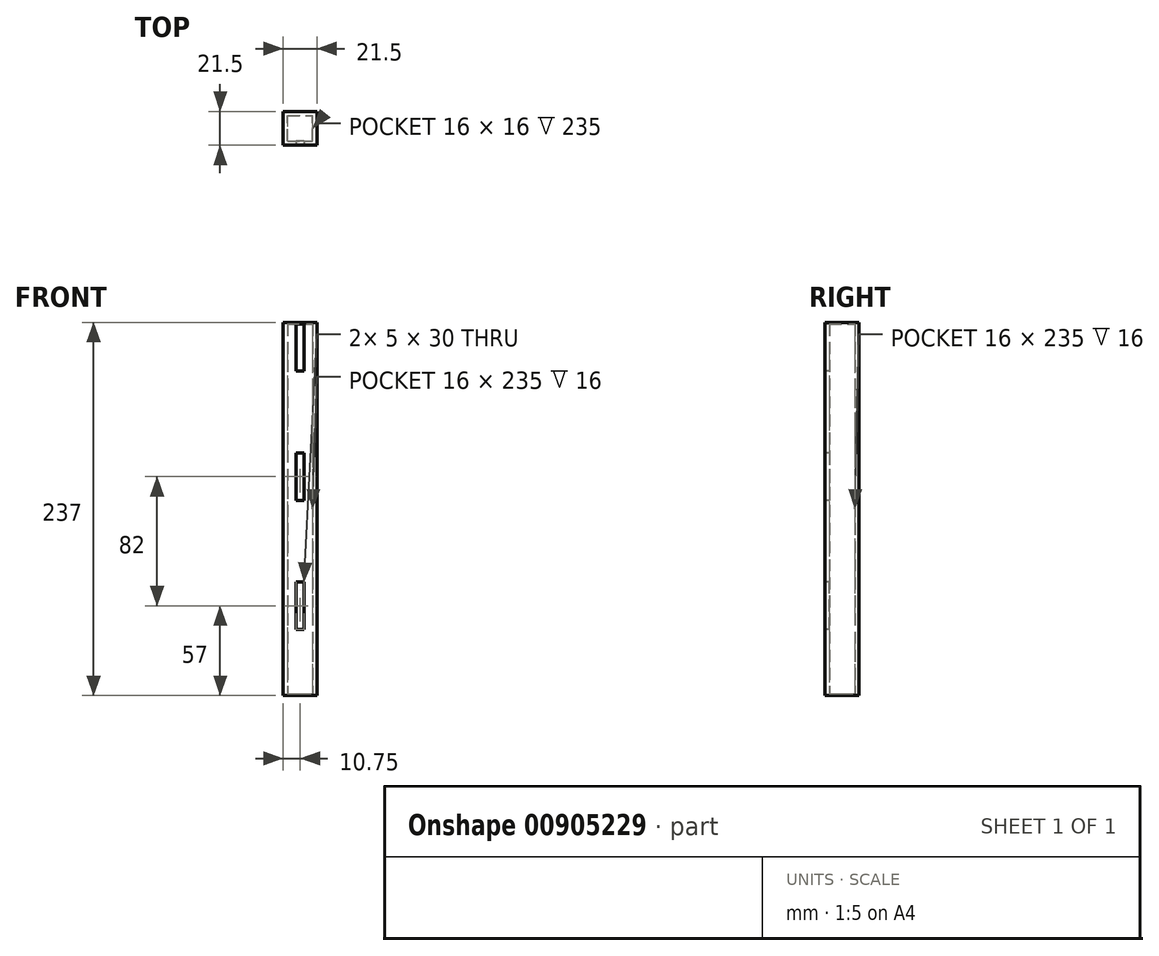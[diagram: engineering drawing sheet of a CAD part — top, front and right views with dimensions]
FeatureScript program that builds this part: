
annotation { "Feature Type Name" : "Feature", "Feature Type Description" : "" }
export const myFeature = defineFeature(function(context is Context, id is Id, definition is map)
    precondition{}
    {
        {
            var Q0;
            Q0=qCreatedBy(makeId("Top.planeOp"),FACE);
            var sketch = newSketch(context, id + "F0", { "sketchPlane" : qUnion([Q0])});
            skLineSegment(sketch, "E0.bottom", {"start": v(-21.5, 21.5) * mm, "end": v(0, 21.5) * mm});
            skLineSegment(sketch, "E0.top", {"start": v(-21.5, 0) * mm, "end": v(0, 0) * mm});
            skLineSegment(sketch, "E0.left", {"start": v(-21.5, 21.5) * mm, "end": v(-21.5, 0) * mm});
            skLineSegment(sketch, "E0.right", {"start": v(0, 21.5) * mm, "end": v(0, 0) * mm});
            skLineSegment(sketch, "E1.bottom", {"start": v(-18.75, 18.75) * mm, "end": v(-2.75, 18.75) * mm});
            skLineSegment(sketch, "E1.top", {"start": v(-18.75, 2.75) * mm, "end": v(-2.75, 2.75) * mm});
            skLineSegment(sketch, "E1.left", {"start": v(-18.75, 18.75) * mm, "end": v(-18.75, 2.75) * mm});
            skLineSegment(sketch, "E1.right", {"start": v(-2.75, 18.75) * mm, "end": v(-2.75, 2.75) * mm});
            skSolve(sketch);
        }
        {
            var Q0;
            Q0=makeQuery(id+"F0.imprint","IMPRINT",FACE,{"disambiguationData":[TD([[makeQuery(id+"F0.imprint","IMPRINT",EDGE,{"derivedFrom":sQuery(id+"F0.wireOp",EDGE,"E0.bottom")}),-1.0]])]});
            var Q1;
            Q1=makeQuery(id+"F0.imprint","IMPRINT",FACE,{"disambiguationData":[TD([[makeQuery(id+"F0.imprint","IMPRINT",EDGE,{"derivedFrom":sQuery(id+"F0.wireOp",EDGE,"E1.bottom")}),-1.0]])]});
            extrude(context, id + "F1", {"entities" : qUnion([Q0, Q1]), "depth" : 237 * mm, "offsetDistance" : 25 * mm});
        }
        {
            var Q0;
            Q0=makeQuery(id+"F1.opExtrude","SWEPT_FACE",FACE,{"disambiguationData":[OSD([sQuery(id+"F0.wireOp",EDGE,"E0.top")])]});
            var sketch = newSketch(context, id + "F2", { "sketchPlane" : qUnion([Q0])});
            skLineSegment(sketch, "E2.bottom", {"start": v(-7.25, 237) * mm, "end": v(-14.25, 237) * mm});
            skLineSegment(sketch, "E2.top", {"start": v(-7.25, 205) * mm, "end": v(-14.25, 205) * mm});
            skLineSegment(sketch, "E2.left", {"start": v(-7.25, 237) * mm, "end": v(-7.25, 205) * mm});
            skLineSegment(sketch, "E2.right", {"start": v(-14.25, 237) * mm, "end": v(-14.25, 205) * mm});
            skLineSegment(sketch, "E3.bottom", {"start": v(-8.25, 236) * mm, "end": v(-13.25, 236) * mm});
            skLineSegment(sketch, "E3.top", {"start": v(-8.25, 206) * mm, "end": v(-13.25, 206) * mm});
            skLineSegment(sketch, "E3.left", {"start": v(-8.25, 236) * mm, "end": v(-8.25, 206) * mm});
            skLineSegment(sketch, "E3.right", {"start": v(-13.25, 236) * mm, "end": v(-13.25, 206) * mm});
            skLineSegment(sketch, "E4", {"start": v(-62.73, 139) * mm, "end": v(121.74, 139) * mm});
            skLineSegment(sketch, "E5.bottom", {"start": v(-14.25, 155) * mm, "end": v(-7.25, 155) * mm});
            skLineSegment(sketch, "E5.top", {"start": v(-14.25, 139) * mm, "end": v(-7.25, 139) * mm});
            skLineSegment(sketch, "E5.left", {"start": v(-14.25, 155) * mm, "end": v(-14.25, 139) * mm});
            skLineSegment(sketch, "E5.right", {"start": v(-7.25, 155) * mm, "end": v(-7.25, 139) * mm});
            skLineSegment(sketch, "E6.bottom", {"start": v(-13.25, 154) * mm, "end": v(-8.25, 154) * mm});
            skLineSegment(sketch, "E6.top", {"start": v(-13.25, 139) * mm, "end": v(-8.25, 139) * mm});
            skLineSegment(sketch, "E6.left", {"start": v(-13.25, 154) * mm, "end": v(-13.25, 139) * mm});
            skLineSegment(sketch, "E6.right", {"start": v(-8.25, 154) * mm, "end": v(-8.25, 139) * mm});
            skLineSegment(sketch, "E7.MirrorCS", {"start": v(-7.25, 41) * mm, "end": v(-7.25, 73) * mm});
            skLineSegment(sketch, "E8.MirrorCS", {"start": v(-7.25, 73) * mm, "end": v(-14.25, 73) * mm});
            skLineSegment(sketch, "E9.MirrorCS", {"start": v(-7.25, 41) * mm, "end": v(-14.25, 41) * mm});
            skLineSegment(sketch, "E10.MirrorCS", {"start": v(-14.25, 41) * mm, "end": v(-14.25, 73) * mm});
            skLineSegment(sketch, "E11.MirrorCS", {"start": v(-8.25, 72) * mm, "end": v(-13.25, 72) * mm});
            skLineSegment(sketch, "E12.MirrorCS", {"start": v(-13.25, 42) * mm, "end": v(-13.25, 72) * mm});
            skLineSegment(sketch, "E13.MirrorCS", {"start": v(-8.25, 42) * mm, "end": v(-8.25, 72) * mm});
            skLineSegment(sketch, "E14.MirrorCS", {"start": v(-8.25, 42) * mm, "end": v(-13.25, 42) * mm});
            skLineSegment(sketch, "E15.MirrorCS", {"start": v(-8.25, 124) * mm, "end": v(-8.25, 139) * mm});
            skLineSegment(sketch, "E16.MirrorCS", {"start": v(-13.25, 124) * mm, "end": v(-8.25, 124) * mm});
            skLineSegment(sketch, "E17.MirrorCS", {"start": v(-14.25, 123) * mm, "end": v(-14.25, 139) * mm});
            skLineSegment(sketch, "E18.MirrorCS", {"start": v(-14.25, 123) * mm, "end": v(-7.25, 123) * mm});
            skLineSegment(sketch, "E19.MirrorCS", {"start": v(-7.25, 123) * mm, "end": v(-7.25, 139) * mm});
            skLineSegment(sketch, "E20.MirrorCS", {"start": v(-13.25, 124) * mm, "end": v(-13.25, 139) * mm});
            skSolve(sketch);
        }
        {
            var Q0;
            Q0=makeQuery(id+"F2.imprint","IMPRINT",FACE,{"disambiguationData":[TD([[makeQuery(id+"F2.imprint","IMPRINT",EDGE,{"derivedFrom":sQuery(id+"F2.wireOp",EDGE,"E3.bottom")}),1.0]])]});
            var Q1;
            Q1=makeQuery(id+"F2.imprint","IMPRINT",FACE,{"disambiguationData":[TD([[makeQuery(id+"F2.imprint","IMPRINT",EDGE,{"derivedFrom":sQuery(id+"F2.wireOp",EDGE,"E6.bottom")}),-1.0]])]});
            var Q2;
            Q2=makeQuery(id+"F2.imprint","IMPRINT",FACE,{"disambiguationData":[TD([[makeQuery(id+"F2.imprint","IMPRINT",EDGE,{"derivedFrom":sQuery(id+"F2.wireOp",EDGE,"E15.MirrorCS")}),1.0]])]});
            var Q3;
            Q3=makeQuery(id+"F2.imprint","IMPRINT",FACE,{"disambiguationData":[TD([[makeQuery(id+"F2.imprint","IMPRINT",EDGE,{"derivedFrom":sQuery(id+"F2.wireOp",EDGE,"E11.MirrorCS")}),1.0]])]});
            extrude(context, id + "F3", {"entities" : qUnion([Q0, Q1, Q2, Q3]), "operationType" : NewBodyOperationType.REMOVE, "oppositeDirection" : true, "depth" : 2.75 * mm, "offsetDistance" : 25 * mm});
        }
        {
            var Q0;
            Q0=makeQuery(id+"F1.opExtrude","CAP_FACE",FACE,{"disambiguationData":[OSD([sQuery(id+"F0.wireOp",EDGE,"E0.bottom"),sQuery(id+"F0.wireOp",EDGE,"E0.top"),sQuery(id+"F0.wireOp",EDGE,"E0.left"),sQuery(id+"F0.wireOp",EDGE,"E0.right")])],"isStart":true});
            var sketch = newSketch(context, id + "F4", { "sketchPlane" : qUnion([Q0])});
            skLineSegment(sketch, "E21.bottom", {"start": v(-18.75, -2.75) * mm, "end": v(-2.75, -2.75) * mm});
            skLineSegment(sketch, "E21.top", {"start": v(-18.75, -18.75) * mm, "end": v(-2.75, -18.75) * mm});
            skLineSegment(sketch, "E21.left", {"start": v(-18.75, -2.75) * mm, "end": v(-18.75, -18.75) * mm});
            skLineSegment(sketch, "E21.right", {"start": v(-2.75, -2.75) * mm, "end": v(-2.75, -18.75) * mm});
            skSolve(sketch);
        }
        {
            var Q0;
            Q0=makeQuery(id+"F4.imprint","IMPRINT",FACE,{"disambiguationData":[TD([[makeQuery(id+"F4.imprint","IMPRINT",EDGE,{"derivedFrom":sQuery(id+"F4.wireOp",EDGE,"E21.bottom")}),-1.0]])]});
            extrude(context, id + "F5", {"entities" : qUnion([Q0]), "operationType" : NewBodyOperationType.REMOVE, "oppositeDirection" : true, "depth" : 236 * mm, "offsetDistance" : 25 * mm});
        }
        {
            var Q0;
            Q0=makeQuery(id+"F1.opExtrude","CAP_FACE",FACE,{"disambiguationData":[OSD([sQuery(id+"F0.wireOp",EDGE,"E0.bottom"),sQuery(id+"F0.wireOp",EDGE,"E0.top"),sQuery(id+"F0.wireOp",EDGE,"E0.left"),sQuery(id+"F0.wireOp",EDGE,"E0.right")])],"isStart":true});
            var sketch = newSketch(context, id + "F6", { "sketchPlane" : qUnion([Q0])});
            skLineSegment(sketch, "E22.bottom", {"start": v(-18.75, -2.75) * mm, "end": v(-2.75, -2.75) * mm});
            skLineSegment(sketch, "E22.top", {"start": v(-18.75, -18.75) * mm, "end": v(-2.75, -18.75) * mm});
            skLineSegment(sketch, "E22.left", {"start": v(-18.75, -2.75) * mm, "end": v(-18.75, -18.75) * mm});
            skLineSegment(sketch, "E22.right", {"start": v(-2.75, -2.75) * mm, "end": v(-2.75, -18.75) * mm});
            skSolve(sketch);
        }
        {
            var Q0;
            Q0=makeQuery(id+"F6.imprint","IMPRINT",FACE,{"disambiguationData":[TD([[makeQuery(id+"F6.imprint","IMPRINT",EDGE,{"derivedFrom":sQuery(id+"F6.wireOp",EDGE,"E22.bottom")}),-1.0]])]});
            extrude(context, id + "F7", {"entities" : qUnion([Q0]), "operationType" : NewBodyOperationType.ADD, "oppositeDirection" : true, "depth" : 1 * mm, "offsetDistance" : 25 * mm});
        }
    });
